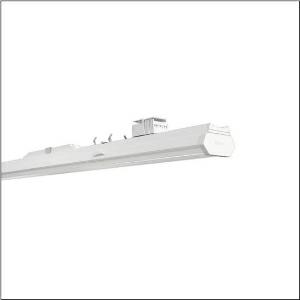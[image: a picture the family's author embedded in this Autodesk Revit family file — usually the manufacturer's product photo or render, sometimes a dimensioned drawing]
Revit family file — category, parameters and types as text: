
# Revit family: licross_r__11_protected_extreme_ho_51tp12dn6e5me_8bd9
name_source: partatom
category: Lighting Fixtures
units: mm (PartAtom-declared; Revit-internal decimal feet)

## family parameters
Cut with Voids When Loaded = No
Host = Face
Light Source = No
Part Type = Normal
Room Calculation Point = No
Round Connector Dimension = Use Diameter
Shared = No

## types (1)
- --- (1 x LED, 14910 lm, 87.3 W, 6500K)
    Apparent Load = 87 VA
    CIE Flux Codes = 70 91 97 98 100
    Color Rendering = 80
    Color Temperature = 6500K
    Default Elevation = 1800 mm
    Description = Licross® 11 Protected extreme HO, luminaire insert, of sheet steel, galvanised, coil coated, white, length: 1.500mm, width: 90mm, height: 101mm, LED rated luminous flux: 14.910lm, light colour: 865, control gear: DALI 2, with plug, 5-pole, with phase selection, mains connection: 220..240V, AC, 50/60Hz, rated input power: 87W, halogen-free wiring, primary optical cover: cover, of PMMA, light emission: direct distribution, primary light characteristic: symmetric, protection rating (complete): IP64, insulation class (complete): insulation class I (protective earthing), certification: CE, ENEC, VDE, UKCA, protection symbol: D if used in an environment with conductive dust loads with corresponding accessories, impact resistance: IK06, permissible ambient temperature for indoor applications: -40..+40°C, LABS conformity tested according to VDMA 24364:2018-05, reducing of maximum allowable ambient temperature of 5°C with ceiling mounting, corresponds to IFS (International Featured Standards) requirements for safety and quality in the food industry, packaging unit: 1 piece
    Height = 92 mm
    Lamp = 1 x LED
    Lamp Light Flux = 14910 lm
    Lamp Power = 87.3 W
    Lamp count = 1
    Length = 1500 mm
    Luminous efficacy = 171 lm/W
    Manufacturer = Siteco
    ModVariant = No
    Model = 51TP12DN6E5ME
    Mounting Place = Ceiling
    Mounting Type = Pendant
    Number of Poles = 1
    OnlyDefault = Yes
    Power Factor = 1
    Product Name = Licross® 11 Protected extreme HO
    Product group = luminaire insert
    ProductGroupID = 902
    Protection Class = Protection class I
    Protection Degree = IP 64
    RLX_Detail_Level = 1
    RLX_Emergency_Light_Flux = 0 lm
    RLX_Emergency_Type = 0
    RLX_Emergency_Type_DB = No
    RlxData = <blob elided: 24377 chars, md5=34411415>
    Socket = socket
    Standby Power = 0 W
    System Light Flux = 14910 lm
    System Power = 87 W
    Type Comments = factory setting: luminous flux: 100 % | dim-lin: 254 | 589 mA
    Type Image = l_1256148.jpg
    URL = http://relux.com
    VarID = @adj_010549
    Voltage = 0 V
    Weight = 0.00 kg
    Width = 88 mm

## geometry (parser evidence)
native form markers: Blend x4, Sweep x10
no freeform markers — native parametric forms only
